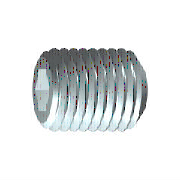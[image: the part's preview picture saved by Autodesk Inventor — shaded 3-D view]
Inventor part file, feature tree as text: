
AUTODESK INVENTOR PART (.ipt)
format: ipt  version: 2024.1 (Build 281209000, 209)  size: 166,400 bytes
history: native  units: mm (DEFAULTED — no unit token found)
features: extrude x1, other x1, plane x1
ambient origin geometry x8: Origin, YZ Plane, XZ Plane, XY Plane, X Axis, Y Axis, Z Axis, Center Point
bodies: Solid1 (feature_tree), Body (feature_tree)
feature tree (3):
  extrude  "Slot"  Depth=2.0mm
  other  "Work Axis1"
  plane  "Work Plane1"
